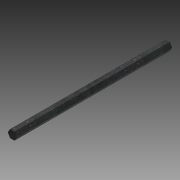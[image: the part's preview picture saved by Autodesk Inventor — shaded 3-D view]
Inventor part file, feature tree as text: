
AUTODESK INVENTOR PART (.ipt)
format: ipt  version: 2014 SP1 (Build 180222100, 222)  size: 86,528 bytes
history: native  units: in
note: dims shown in document units (in); Inventor stores cm internally (conversion verified against a paired STEP export)
features: extrude x1, sketch x1
ambient origin geometry x8: Origin, YZ Plane, XZ Plane, XY Plane, X Axis, Y Axis, Z Axis, Center Point
bodies: Solid1 (feature_tree)
feature tree (2):
  extrude  "Extrusion1"  Depth=10.0in TaperAngle=0.0deg
  sketch  "Sketch1"  dims[d0=0.5in d1=10.0in d2=0.0in]
